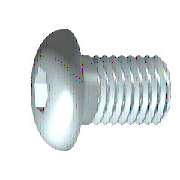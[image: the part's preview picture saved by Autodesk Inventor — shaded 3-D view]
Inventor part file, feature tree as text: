
AUTODESK INVENTOR PART (.ipt)
format: ipt  version: 2015 (Build 190159000, 159)  size: 203,776 bytes
history: native  units: mm (DEFAULTED — no unit token found)
features: sketch x2, extrude x1, plane x1, fillet x1
ambient origin geometry x7: Origin, YZ Plane, XY Plane, X Axis, Y Axis, Z Axis, Center Point
bodies: Solid1 (feature_tree), Body (feature_tree)
feature tree (5):
  extrude  "Slot"  Depth=2.5654mm
  plane  "Work Plane1"
  fillet  "Fillet2"  Radius=2.5654mm
  sketch  "Sketch1"  dims[d1=7.4166mm d2=2.1083mm d3=2.5654mm]
  sketch  "Sketch2"  dims[d4=1.778mm d5=60.0deg d6=4.826mm d7=4.826mm d8=3.666174mm d9=9.1694mm d10=90.0deg d11=10.0mm d12=0.0mm d13=7.4166mm d14=0.0mm d15=0.649224mm d16=0.649224mm d17=2.3114mm d19=0.0mm d26=9.525mm d27=45.0deg d28=0.0mm d29=0.0mm d30=0.1mm]
